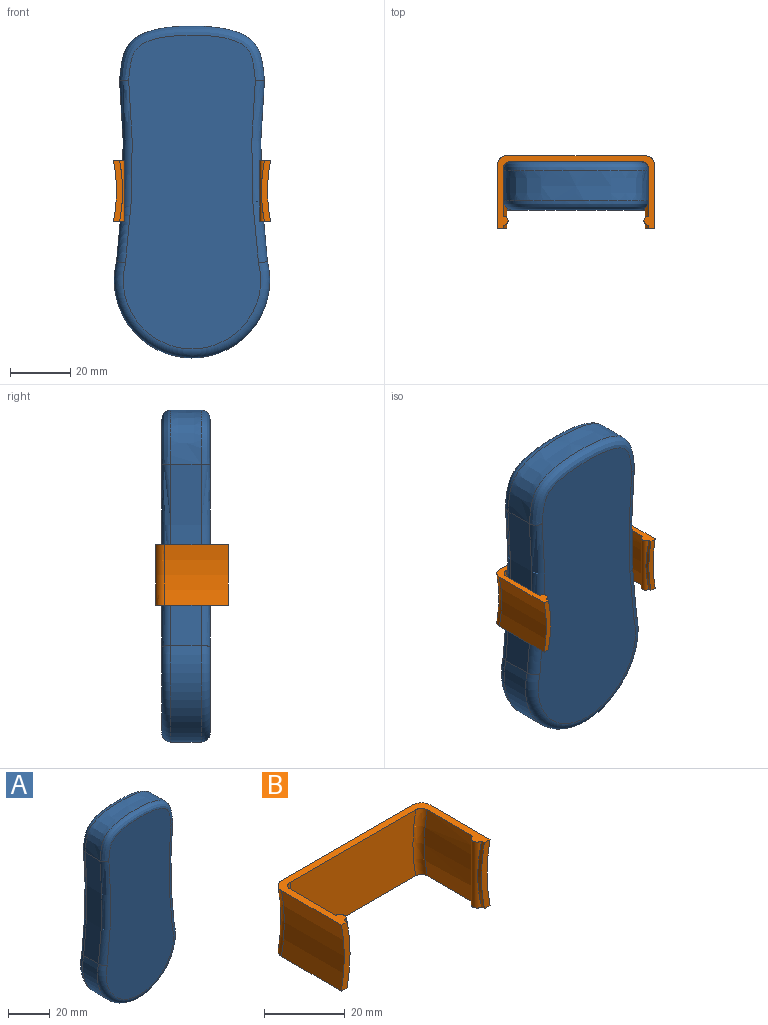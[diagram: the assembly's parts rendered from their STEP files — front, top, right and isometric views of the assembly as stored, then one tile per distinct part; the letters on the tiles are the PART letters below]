
ASSEMBLY  parts=2 mates=1
PART A: 14 faces, bbox 55.8x16x112.1 mm
  f0: extruded ~48x18mm, area 699.3mm2, adj f1,f3,f7,f10
  f1: cylinder r=264.32mm len=60mm, axis (0,1,0), area 601.4mm2, adj f0,f2,f6,f11
  f2: cylinder r=25.77mm len=51.53mm, axis (0,1,0), area 935.4mm2, adj f1,f3,f8,f13
  f3: cylinder r=264.32mm len=60mm, axis (0,1,0), area 601.4mm2, adj f0,f2,f9,f12
  f4: plane 104x45.53mm, normal (0,-1,0), area 4083.9mm2, adj f6,f7,f8,f9
  f5: plane 104x45.53mm, normal (0,1,0), area 4084.1mm2, adj f10,f11,f12,f13
  f6: torus R=267.32mm, axis (0,-1,0), area 284.3mm2, adj f1,f4,f7,f8
  f7: bspline ~48.43x22.62mm, area 313.1mm2, adj f0,f4,f6,f9
  f8: torus R=22.77mm, axis (0,-1,0), area 423mm2, adj f2,f4,f6,f9
  f9: torus R=267.32mm, axis (0,-1,0), area 284.3mm2, adj f3,f4,f7,f8
  f10: bspline ~48.43x22.62mm, area 313.1mm2, adj f0,f5,f11,f12
  f11: torus R=267.32mm, axis (0,-1,0), area 284.3mm2, adj f1,f5,f10,f13
  f12: torus R=267.32mm, axis (0,-1,0), area 284.3mm2, adj f3,f5,f10,f13
  f13: torus R=22.77mm, axis (0,-1,0), area 423mm2, adj f2,f5,f11,f12
PART B: 18 faces, bbox 52x24x23.8 mm
  f0: cylinder r=50.5mm len=20mm, axis (0,1,0), area 24.1mm2, adj f4,f6,f11,f15
  f1: cylinder r=50.5mm len=20mm, axis (0,1,0), area 326.1mm2, adj f4,f6,f12,f15
  f2: cylinder r=50.5mm len=20mm, axis (0,1,0), area 24.1mm2, adj f4,f6,f10,f14
  f3: cylinder r=50.5mm len=21mm, axis (0,1,0), area 422.8mm2, adj f4,f6,f11,f16
  f4: plane 52x24mm, normal (0,0,1), area 196.9mm2, adj f0,f1,f2,f3,f5,f7,f8,f9
  f5: cylinder r=50.5mm len=21mm, axis (0,1,0), area 422.8mm2, adj f4,f6,f10,f17
  f6: plane 52x24mm, normal (0,0,-1), area 196.9mm2, adj f0,f1,f2,f3,f5,f7,f8,f9
  f7: plane 43.92x20mm, normal (0,-1,0), area 852.8mm2, adj f4,f6,f12,f13
  f8: plane 45.89x20mm, normal (0,1,0), area 892.5mm2, adj f4,f6,f16,f17
  f9: cylinder r=50.5mm len=20mm, axis (0,1,0), area 326.1mm2, adj f4,f6,f13,f14
  f10: plane 20x3mm, normal (0,-1,0), area 40mm2, adj f2,f4,f5,f6
  f11: plane 20x3mm, normal (0,-1,0), area 40mm2, adj f0,f3,f4,f6
  f12: torus R=52.5mm, axis (0,-1,0), area 63.2mm2, adj f1,f4,f6,f7
  f13: torus R=52.5mm, axis (0,-1,0), area 63.2mm2, adj f4,f6,f7,f9
  f14: cylinder r=1.5mm len=20mm, axis (0,0,-1), area 65.9mm2, adj f2,f4,f6,f9
  f15: cylinder r=1.5mm len=20mm, axis (0,0,-1), area 65.9mm2, adj f0,f1,f4,f6
  f16: torus R=53.5mm, axis (0,-1,0), area 94.8mm2, adj f3,f4,f6,f8
  f17: torus R=53.5mm, axis (0,-1,0), area 94.8mm2, adj f4,f5,f6,f8
PLACE A t=(-46.83,33.43,-5.99)mm fixed
PLACE B t=(-47.83,35.43,39.37)mm
MATE fastened A.f5 <-> B.f7  axis (0,1,0) through (-21.83,33.43,49.37)mm
